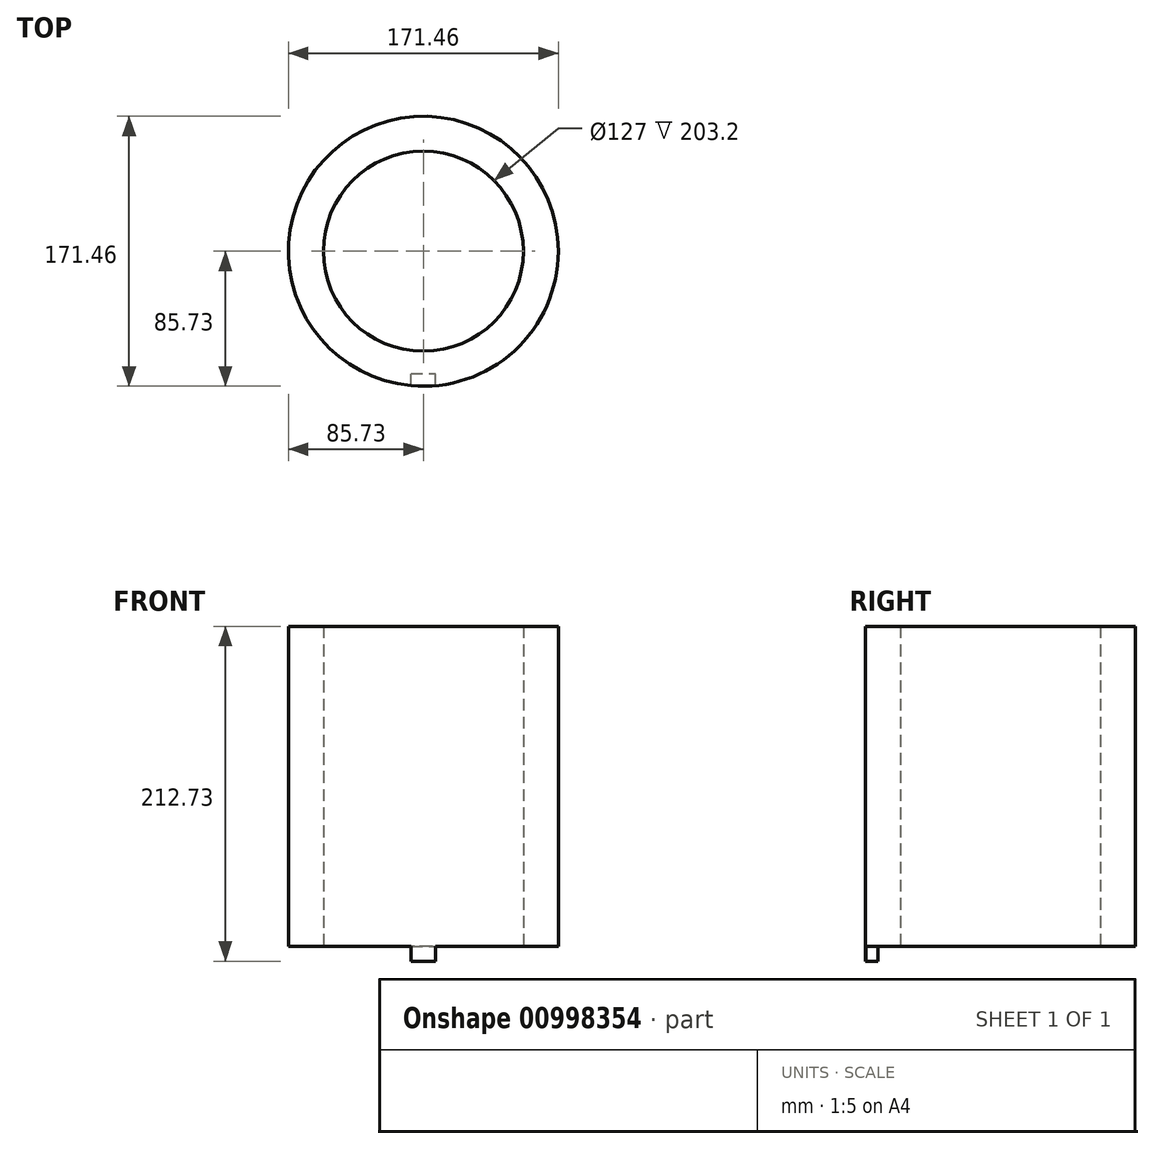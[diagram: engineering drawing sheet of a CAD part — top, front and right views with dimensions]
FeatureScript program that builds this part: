
annotation { "Feature Type Name" : "Feature", "Feature Type Description" : "" }
export const myFeature = defineFeature(function(context is Context, id is Id, definition is map)
    precondition{}
    {
        {
            var Q0;
            Q0=qCreatedBy(makeId("Top.planeOp"),FACE);
            var sketch = newSketch(context, id + "F0", { "sketchPlane" : qUnion([Q0])});
            skCircle(sketch, "E0", {"center": v(0, 0) * mm, "radius": 63.5 * mm});
            skCircle(sketch, "E1", {"center": v(0, 0) * mm, "radius": 85.73 * mm});
            skSolve(sketch);
        }
        {
            var Q0;
            Q0 = qSketchRegion(id + "F0", true);
            extrude(context, id + "F1", {"entities" : qUnion([Q0]), "depth" : 203.2 * mm, "offsetDistance" : 25.4 * mm});
        }
        {
            var Q0;
            Q0=makeQuery(id+"F1.opExtrude","CAP_FACE",FACE,{"disambiguationData":[OSD([sQuery(id+"F0.wireOp",EDGE,"E0"),sQuery(id+"F0.wireOp",EDGE,"E1")])],"isStart":true});
            var sketch = newSketch(context, id + "F2", { "sketchPlane" : qUnion([Q0])});
            skLineSegment(sketch, "E2.top", {"start": v(-7.87, 77.74) * mm, "end": v(7.87, 77.74) * mm});
            skLineSegment(sketch, "E2.left", {"start": v(-7.87, 85.36) * mm, "end": v(-7.87, 77.74) * mm});
            skLineSegment(sketch, "E2.right", {"start": v(7.87, 85.36) * mm, "end": v(7.87, 77.74) * mm});
            skArc(sketch, "E3", {"start": v(7.87, 85.36) * mm, "mid": v(0, 85.73) * mm, "end": v(-7.87, 85.36) * mm});
            skSolve(sketch);
        }
        {
            var Q0;
            Q0 = qSketchRegion(id + "F2", true);
            extrude(context, id + "F3", {"entities" : qUnion([Q0]), "operationType" : NewBodyOperationType.ADD, "depth" : 9.52 * mm, "offsetDistance" : 25.4 * mm});
        }
    });
